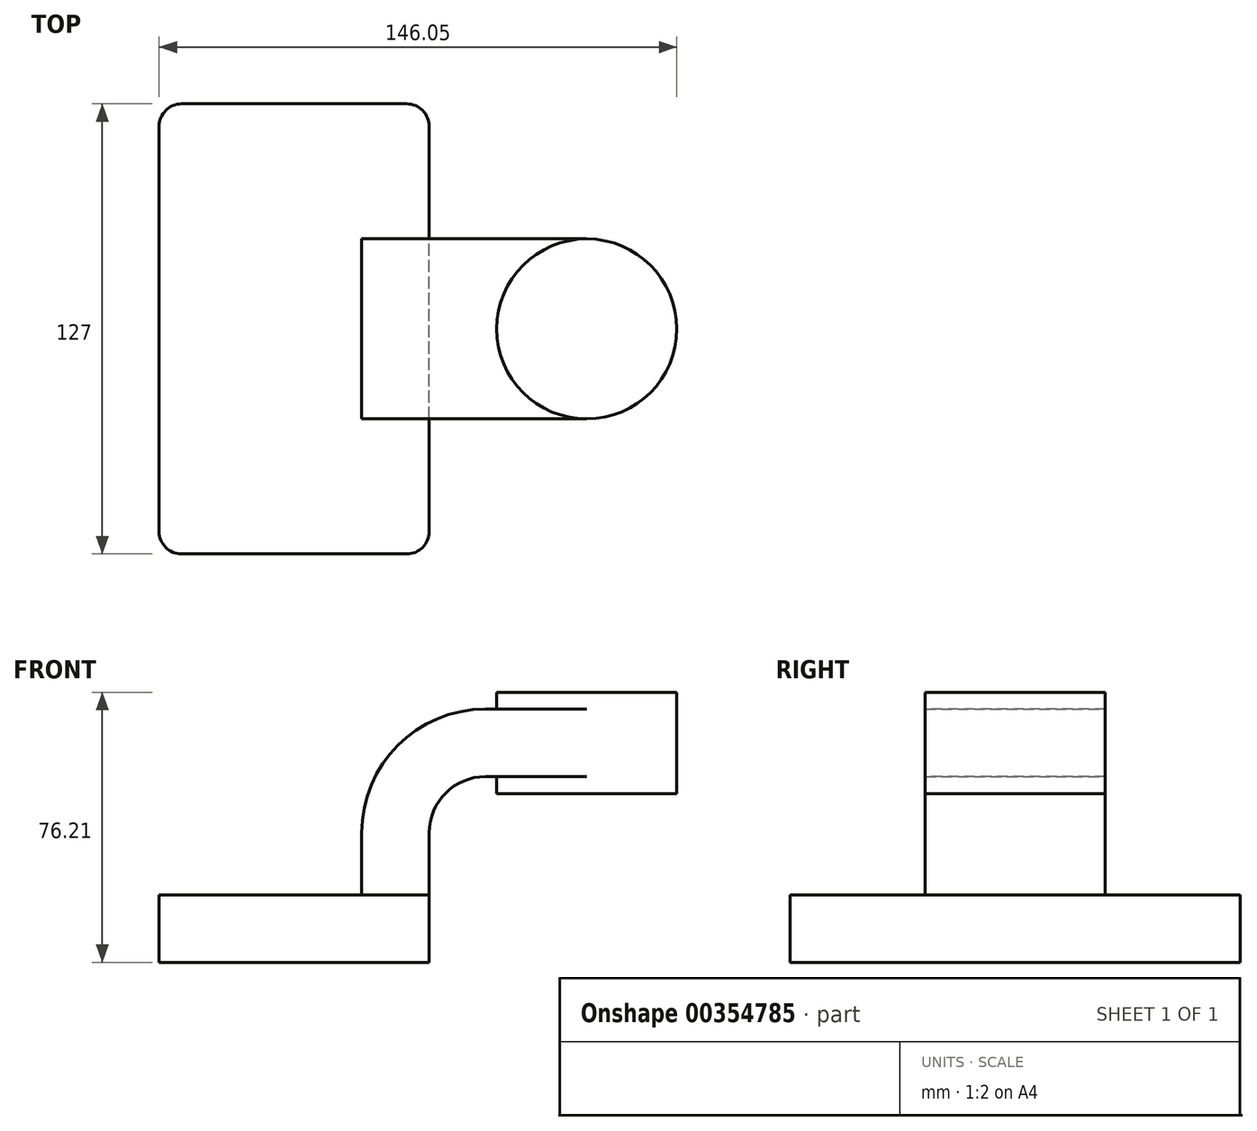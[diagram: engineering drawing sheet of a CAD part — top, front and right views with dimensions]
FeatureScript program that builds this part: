
annotation { "Feature Type Name" : "Feature", "Feature Type Description" : "" }
export const myFeature = defineFeature(function(context is Context, id is Id, definition is map)
    precondition{}
    {
        {
            var Q0;
            Q0=qCreatedBy(makeId("Front.planeOp"),FACE);
            var sketch = newSketch(context, id + "F0", { "sketchPlane" : qUnion([Q0])});
            skLineSegment(sketch, "E0.bottom", {"start": v(38.1, 9.53) * mm, "end": v(-38.1, 9.53) * mm});
            skLineSegment(sketch, "E0.top", {"start": v(38.1, -9.52) * mm, "end": v(-38.1, -9.52) * mm});
            skLineSegment(sketch, "E0.left", {"start": v(38.1, 9.53) * mm, "end": v(38.1, -9.52) * mm});
            skLineSegment(sketch, "E0.right", {"start": v(-38.1, 9.53) * mm, "end": v(-38.1, -9.52) * mm});
            skPoint(sketch, "E0.middle", {"position": v(0, 0) * mm});
            skLineSegment(sketch, "E1.bottom", {"start": v(107.95, 66.68) * mm, "end": v(57.15, 66.68) * mm});
            skLineSegment(sketch, "E1.top", {"start": v(107.95, 38.1) * mm, "end": v(57.15, 38.1) * mm});
            skLineSegment(sketch, "E1.left", {"start": v(107.95, 66.68) * mm, "end": v(107.95, 38.1) * mm});
            skLineSegment(sketch, "E1.right", {"start": v(57.15, 66.67) * mm, "end": v(57.15, 38.1) * mm});
            skPoint(sketch, "E1.middle", {"position": v(82.55, 52.39) * mm});
            skLineSegment(sketch, "E2", {"start": v(38.1, 9.53) * mm, "end": v(38.1, 27) * mm});
            skArc(sketch, "E3", {"start": v(38.1, 27) * mm, "mid": v(42.75, 38.23) * mm, "end": v(53.97, 42.88) * mm});
            skLineSegment(sketch, "E4", {"start": v(53.97, 42.88) * mm, "end": v(82.55, 42.88) * mm});
            skLineSegment(sketch, "E5.0", {"start": v(53.97, 61.93) * mm, "end": v(82.55, 61.93) * mm});
            skArc(sketch, "E5.1", {"start": v(19.05, 27) * mm, "mid": v(29.28, 51.7) * mm, "end": v(53.97, 61.93) * mm});
            skLineSegment(sketch, "E5.2", {"start": v(19.05, 9.53) * mm, "end": v(19.05, 27) * mm});
            skFitSpline(sketch, "E6", {"points": [v(-38.1, 9.53) * mm, v(53.97, 61.93) * mm], "startDerivative": vector(0, 94.62) * mm, "endDerivative": vector(161.92, -9.1) * mm});
            skPoint(sketch, "E7", {"position": v(-38.1, 0) * mm});
            skLineSegment(sketch, "E8", {"start": v(82.55, 66.68) * mm, "end": v(82.55, 38.1) * mm});
            skSolve(sketch);
        }
        {
            var Q0;
            Q0=makeQuery(id+"F0.imprint","IMPRINT",FACE,{"disambiguationData":[TD([[makeQuery(id+"F0.imprint","IMPRINT",EDGE,{"derivedFrom":sQuery(id+"F0.wireOp",EDGE,"E0.top")}),-1.0]])]});
            extrude(context, id + "F1", {"entities" : qUnion([Q0]), "endBound" : BoundingType.SYMMETRIC, "depth" : 127 * mm});
        }
        {
            var Q0;
            Q0=makeQuery(id+"F0.imprint","IMPRINT",FACE,{"disambiguationData":[TD([[makeQuery(id+"F0.imprint","IMPRINT",EDGE,{"derivedFrom":sQuery(id+"F0.wireOp",EDGE,"E5.1")}),1.0]])]});
            extrude(context, id + "F2", {"entities" : qUnion([Q0]), "endBound" : BoundingType.SYMMETRIC, "depth" : 15.88 * mm});
        }
        {
            var Q0;
            {var subQ0=sQuery(id+"F0.wireOp",EDGE,"E5.0");var subQ1=sQuery(id+"F0.wireOp",EDGE,"E1.right");var subQ2=makeQuery(id+"F0.imprint","INTERSECT",VERTEX,{"derivedFrom":[subQ1,subQ0]});Q0=makeQuery(id+"F0.imprint","IMPRINT",FACE,{"disambiguationData":[TD([[makeQuery(id+"F0.imprint","IMPRINT",EDGE,{"disambiguationData":[TD([[subQ2,-1.0]])],"derivedFrom":subQ1}),1.0]])]});}
            var Q1;
            {var subQ1=sQuery(id+"F0.wireOp",EDGE,"E2");Q1=makeQuery(id+"F0.imprint","IMPRINT",FACE,{"disambiguationData":[TD([[makeQuery(id+"F0.imprint","IMPRINT",EDGE,{"derivedFrom":subQ1}),1.0]])]});}
            extrude(context, id + "F3", {"entities" : qUnion([Q0, Q1]), "endBound" : BoundingType.SYMMETRIC, "depth" : 50.8 * mm});
        }
        {
            var Q0;
            {var subQ0=sQuery(id+"F0.wireOp",EDGE,"E1.left");Q0=makeQuery(id+"F0.imprint","IMPRINT",FACE,{"disambiguationData":[TD([[makeQuery(id+"F0.imprint","IMPRINT",EDGE,{"derivedFrom":subQ0}),-1.0]])]});}
            var Q1;
            Q1=sQuery(id+"F0.wireOp",EDGE,"E8");
            revolve(context, id + "F4", {"operationType" : NewBodyOperationType.ADD, "entities" : qUnion([Q0]), "axis" : qUnion([Q1]), "revolveType" : RevolveType.FULL});
        }
        {
            var Q0;
            Q0=makeQuery(id+"F1.opExtrude","CAP_EDGE",EDGE,{"disambiguationData":[OSD([sQuery(id+"F0.wireOp",EDGE,"E0.left")])],"isStart":false});
            var Q1;
            Q1=makeQuery(id+"F1.opExtrude","CAP_EDGE",EDGE,{"disambiguationData":[OSD([sQuery(id+"F0.wireOp",EDGE,"E0.right")])],"isStart":false});
            var Q2;
            Q2=makeQuery(id+"F1.opExtrude","CAP_EDGE",EDGE,{"disambiguationData":[OSD([sQuery(id+"F0.wireOp",EDGE,"E0.left")])],"isStart":true});
            var Q3;
            Q3=makeQuery(id+"F1.opExtrude","CAP_EDGE",EDGE,{"disambiguationData":[OSD([sQuery(id+"F0.wireOp",EDGE,"E0.right")])],"isStart":true});
            fillet(context, id + "F5", {"entities" : qUnion([Q0, Q1, Q2, Q3]), "radius" : 6.35 * mm, "tangentPropagation" : true, "allowEdgeOverflow" : false});
        }
    });
